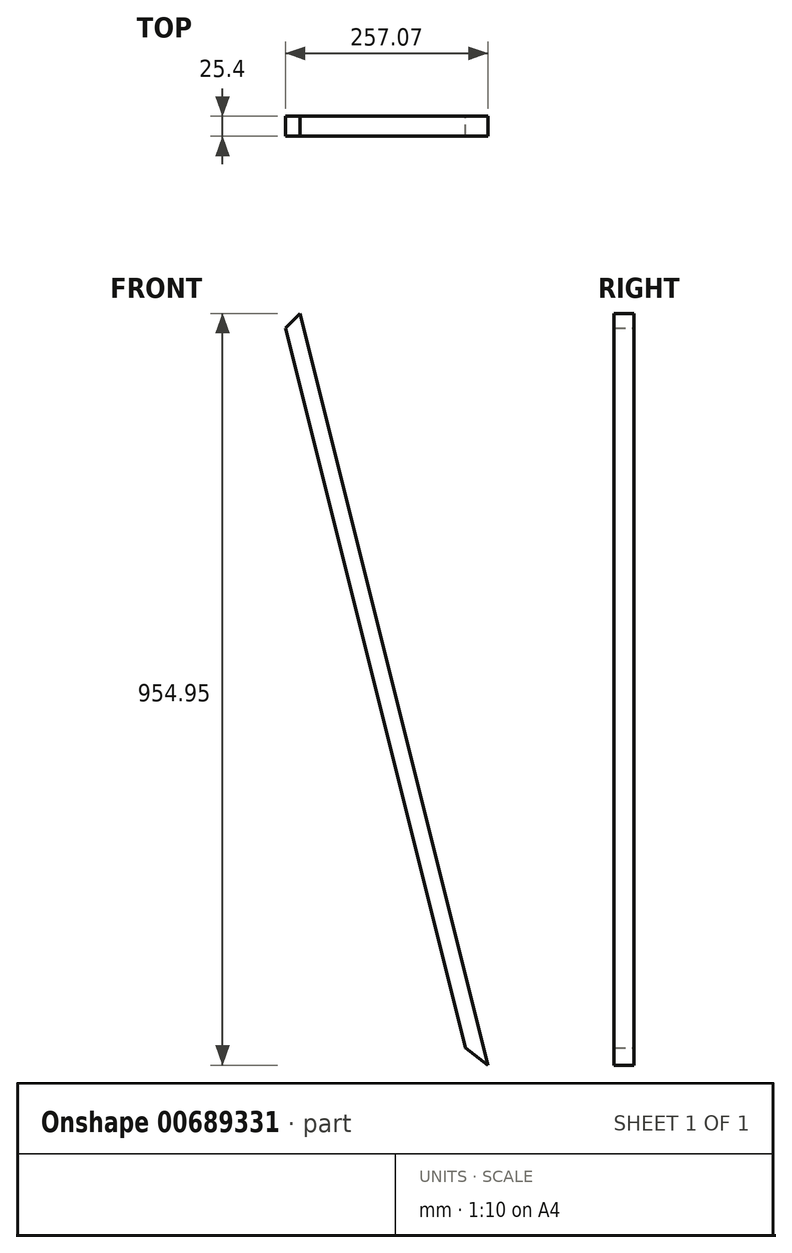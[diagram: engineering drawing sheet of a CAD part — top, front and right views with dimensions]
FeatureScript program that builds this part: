
annotation { "Feature Type Name" : "Feature", "Feature Type Description" : "" }
export const myFeature = defineFeature(function(context is Context, id is Id, definition is map)
    precondition{}
    {
        {
            var Q0;
            Q0=qCreatedBy(makeId("Front.planeOp"),FACE);
            var sketch = newSketch(context, id + "F0", { "sketchPlane" : qUnion([Q0])});
            skLineSegment(sketch, "E0", {"start": v(228.6, -42.72) * mm, "end": v(0, 871.68) * mm});
            skLineSegment(sketch, "E1", {"start": v(0, 871.68) * mm, "end": v(-228.6, -42.72) * mm});
            skLineSegment(sketch, "E2", {"start": v(-228.6, -42.72) * mm, "end": v(228.6, -42.72) * mm});
            skLineSegment(sketch, "E3.0", {"start": v(257.07, -64.94) * mm, "end": v(18.33, 890.01) * mm});
            skLineSegment(sketch, "E4.0", {"start": v(-18.33, 890.01) * mm, "end": v(-257.07, -64.94) * mm});
            skLineSegment(sketch, "E5.0", {"start": v(-257.07, -64.94) * mm, "end": v(257.07, -64.94) * mm});
            skLineSegment(sketch, "E6", {"start": v(0, 871.68) * mm, "end": v(18.33, 890.01) * mm});
            skLineSegment(sketch, "E7", {"start": v(-18.33, 890.01) * mm, "end": v(0, 871.68) * mm});
            skLineSegment(sketch, "E8", {"start": v(-228.6, -42.72) * mm, "end": v(-257.07, -64.94) * mm});
            skLineSegment(sketch, "E9", {"start": v(228.6, -42.72) * mm, "end": v(257.07, -64.94) * mm});
            skLineSegment(sketch, "E10", {"start": v(0, 871.68) * mm, "end": v(0, -42.72) * mm});
            skSolve(sketch);
        }
        {
            var Q0;
            Q0=makeQuery(id+"F0.imprint","IMPRINT",FACE,{"disambiguationData":[TD([[makeQuery(id+"F0.imprint","IMPRINT",EDGE,{"derivedFrom":sQuery(id+"F0.wireOp",EDGE,"E0")}),-1.0]])]});
            extrude(context, id + "F1", {"entities" : qUnion([Q0]), "depth" : 25.4 * mm, "offsetDistance" : 25.4 * mm});
        }
    });
